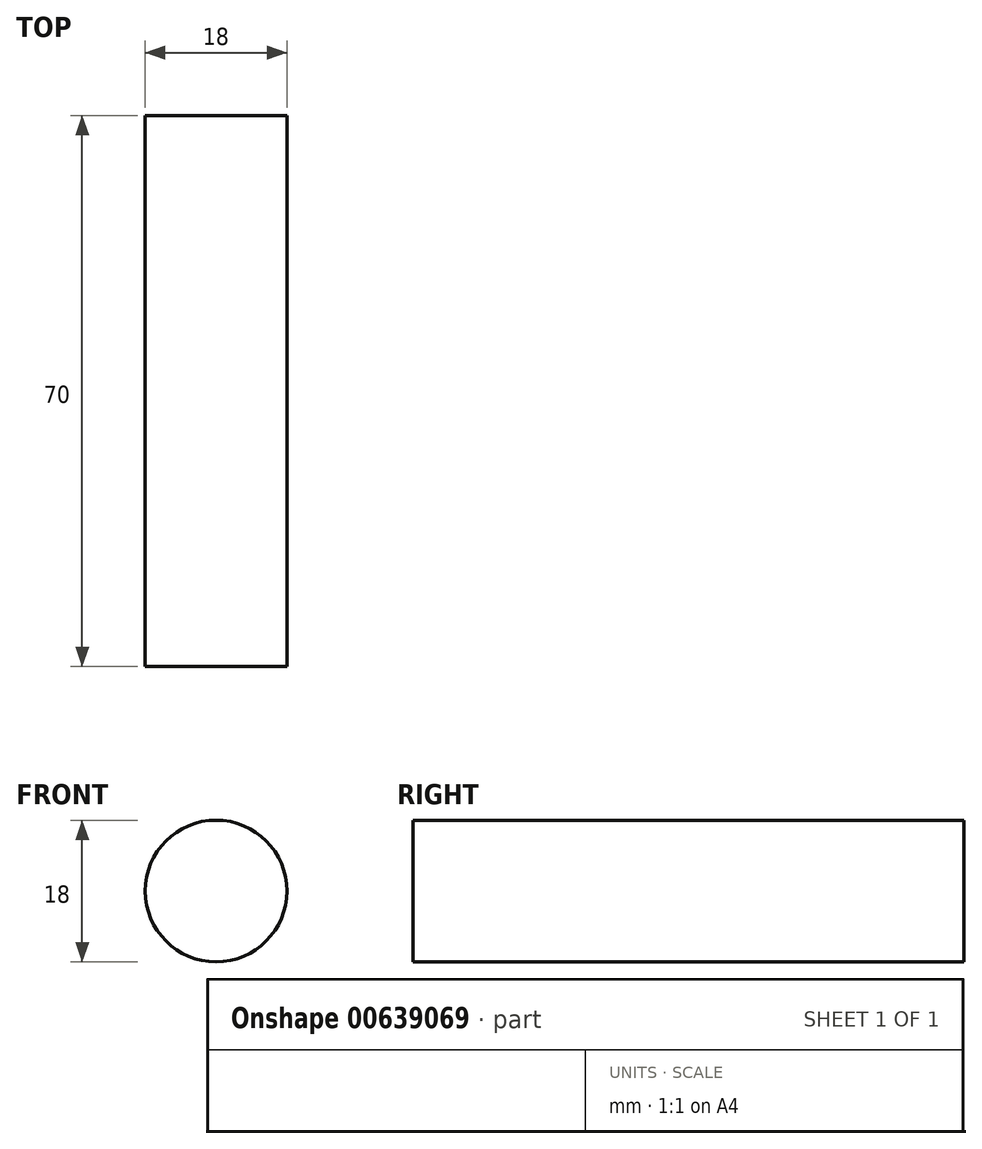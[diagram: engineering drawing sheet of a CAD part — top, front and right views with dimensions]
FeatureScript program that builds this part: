
annotation { "Feature Type Name" : "Feature", "Feature Type Description" : "" }
export const myFeature = defineFeature(function(context is Context, id is Id, definition is map)
    precondition{}
    {
        {
            var Q0;
            Q0=qCreatedBy(makeId("Right.planeOp"),FACE);
            var sketch = newSketch(context, id + "F0", { "sketchPlane" : qUnion([Q0])});
            skLineSegment(sketch, "E0.bottom", {"start": v(35, 0) * mm, "end": v(-35, 0) * mm});
            skLineSegment(sketch, "E0.top", {"start": v(35, -9) * mm, "end": v(-35, -9) * mm});
            skLineSegment(sketch, "E0.left", {"start": v(35, 0) * mm, "end": v(35, -9) * mm});
            skLineSegment(sketch, "E0.right", {"start": v(-35, 0) * mm, "end": v(-35, -9) * mm});
            skPoint(sketch, "E0.middle", {"position": v(0, -4.5) * mm});
            skSolve(sketch);
        }
        {
            var Q0;
            Q0=makeQuery(id+"F0.imprint","IMPRINT",FACE,{"disambiguationData":[TD([[makeQuery(id+"F0.imprint","IMPRINT",EDGE,{"derivedFrom":sQuery(id+"F0.wireOp",EDGE,"E0.bottom")}),1.0]])]});
            var Q1;
            Q1=sQuery(id+"F0.wireOp",EDGE,"E0.bottom");
            revolve(context, id + "F1", {"entities" : qUnion([Q0]), "axis" : qUnion([Q1]), "revolveType" : RevolveType.FULL});
        }
    });
